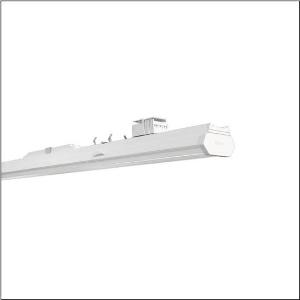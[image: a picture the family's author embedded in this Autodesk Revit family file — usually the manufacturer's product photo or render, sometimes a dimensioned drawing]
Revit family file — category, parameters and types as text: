
# Revit family: licross_r__21_protected_mo_52td11cn49xg_2815
name_source: partatom
category: Lighting Fixtures
units: mm (PartAtom-declared; Revit-internal decimal feet)

## family parameters
Cut with Voids When Loaded = No
Host = Face
Light Source = No
Part Type = Normal
Room Calculation Point = No
Round Connector Dimension = Use Diameter
Shared = No

## types (1)
- --- (1 x LED, 9070 lm, 50.4 W, 4000K)
    Apparent Load = 50 VA
    CIE Flux Codes = 83 94 98 100 100
    Color Rendering = 80
    Color Temperature = 4000K
    Default Elevation = 1800 mm
    Description = Licross® 21 Protected MO, luminaire insert, of sheet steel, galvanised, coil coated, white, length: 1.500mm, width: 90mm, height: 103mm, LED rated luminous flux: 9.080lm, light colour: 840, control gear: ON/OFF Multilumen, CLOi, control gear: ECG Multilumen, with plug, 3-pole, with phase selection, mains connection: 220..240V, AC, 50/60Hz, start of lifetime: 50W, end of service life: 61W, halogen-free wiring, primary light control with lens, of plastic, primary optical cover: cover, of PMMA, light emission: direct distribution, primary light characteristic: symmetric, protection rating (complete): IP54, insulation class (complete): insulation class I (protective earthing), certification: CE, ENEC, VDE, UKCA, protection symbol: D if used in an environment with non-conductive dust loads with corresponding accessories, impact resistance: IK06, permissible ambient temperature for indoor applications: -35..+45°C, corresponds to IFS (International Featured Standards) requirements for safety and quality in the food industry, reducing of maximum allowable ambient temperature of 5°C with ceiling mounting, LABS conformity tested according to VDMA 24364:2018-05, packaging unit: 1 piece
    Height = 92 mm
    Lamp = 1 x LED
    Lamp Light Flux = 9070 lm
    Lamp Power = 50.4 W
    Lamp count = 1
    Length = 1500 mm
    Luminous efficacy = 180 lm/W
    Manufacturer = Siteco
    ModVariant = No
    Model = 52TD11CN49XG
    Mounting Place = Ceiling
    Mounting Type = Pendant
    Number of Poles = 1
    OnlyDefault = Yes
    Power Factor = 1
    Product Name = Licross® 21 Protected MO
    Product group = luminaire insert
    ProductGroupID = 901
    Protection Class = Protection class I
    Protection Degree = IP 54
    RLX_Detail_Level = 1
    RLX_Emergency_Light_Flux = 0 lm
    RLX_Emergency_Type = 0
    RLX_Emergency_Type_DB = No
    RlxData = <blob elided: 21901 chars, md5=971f4d1d>
    Socket = socket
    Standby Power = 0 W
    System Light Flux = 9070 lm
    System Power = 50 W
    Type Comments = factory setting: luminous flux: 100 % | (A | C | E) | 117 mA
    Type Image = l_1256148.jpg
    URL = http://relux.com
    VarID = @adj_059119
    Voltage = 0 V
    Weight = 0.00 kg
    Width = 88 mm

## geometry (parser evidence)
native form markers: Blend x4, Sweep x12
no freeform markers — native parametric forms only
